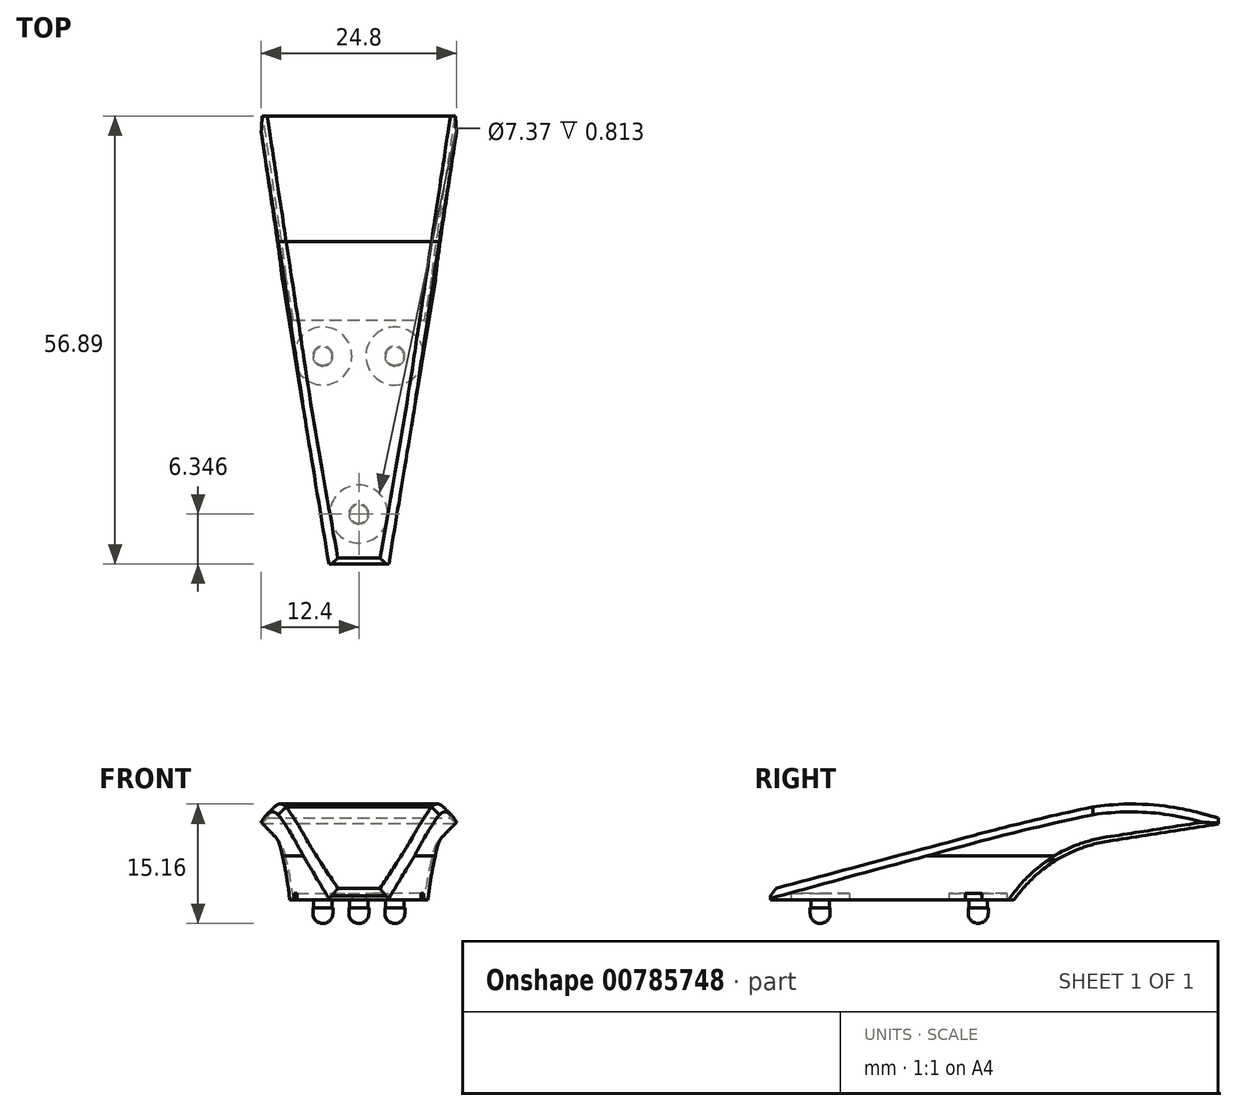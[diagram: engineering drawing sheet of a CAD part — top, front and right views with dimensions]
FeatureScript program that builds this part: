
annotation { "Feature Type Name" : "Feature", "Feature Type Description" : "" }
export const myFeature = defineFeature(function(context is Context, id is Id, definition is map)
    precondition{}
    {
        {
            var Q0;
            Q0=qCreatedBy(makeId("Top.planeOp"),FACE);
            var sketch = newSketch(context, id + "F0", { "sketchPlane" : qUnion([Q0])});
            skPoint(sketch, "E0.middle", {"position": v(0, 0) * mm});
            skLineSegment(sketch, "E1.bottom", {"start": v(3.81, -15.5) * mm, "end": v(-3.8, -15.5) * mm});
            skLineSegment(sketch, "E2", {"start": v(-3.8, -15.5) * mm, "end": v(-8.9, 15.5) * mm});
            skLineSegment(sketch, "E3", {"start": v(3.81, -15.5) * mm, "end": v(8.89, 15.5) * mm});
            skLineSegment(sketch, "E4", {"start": v(-8.9, 15.5) * mm, "end": v(8.89, 15.5) * mm});
            skSolve(sketch);
        }
        {
            var Q0;
            Q0=qCreatedBy(makeId("Front.planeOp"),FACE);
            cPlane(context, id + "F1", {"entities" : qUnion([Q0]), "cplaneType" : CPlaneType.OFFSET, "offset" : 41.4 * mm, "oppositeDirection" : true, "width" : 152.4 * mm, "height" : 152.4 * mm});
        }
        {
            var Q0;
            Q0=qCreatedBy(id+"F1.planeOp",FACE);
            var sketch = newSketch(context, id + "F2", { "sketchPlane" : qUnion([Q0])});
            skLineSegment(sketch, "E5", {"start": v(12.7, 9.65) * mm, "end": v(12.7, 14.22) * mm});
            skLineSegment(sketch, "E6", {"start": v(12.7, 14.22) * mm, "end": v(-12.7, 14.22) * mm});
            skLineSegment(sketch, "E7", {"start": v(-12.7, 14.22) * mm, "end": v(-12.7, 9.65) * mm});
            skLineSegment(sketch, "E8", {"start": v(12.7, 9.65) * mm, "end": v(-12.7, 9.65) * mm});
            skSolve(sketch);
        }
        {
            var Q0;
            Q0 = qSketchRegion(id + "F0", true);
            extrude(context, id + "F3", {"entities" : qUnion([Q0]), "depth" : 5.6 * mm, "offsetDistance" : 25.4 * mm});
        }
        {
            var Q0;
            Q0=makeQuery(id+"F3.opExtrude","CAP_FACE",FACE,{"disambiguationData":[OSD([sQuery(id+"F0.wireOp",EDGE,"E1.bottom"),sQuery(id+"F0.wireOp",EDGE,"E2"),sQuery(id+"F0.wireOp",EDGE,"E3"),sQuery(id+"F0.wireOp",EDGE,"E4")])],"isStart":false});
            var sketch = newSketch(context, id + "F4", { "sketchPlane" : qUnion([Q0])});
            skLineSegment(sketch, "E9", {"start": v(-8.9, 15.5) * mm, "end": v(-3.8, -15.5) * mm});
            skLineSegment(sketch, "E10", {"start": v(-3.8, -15.5) * mm, "end": v(3.81, -15.5) * mm});
            skLineSegment(sketch, "E11", {"start": v(3.81, -15.5) * mm, "end": v(8.89, 15.5) * mm});
            skLineSegment(sketch, "E12", {"start": v(8.89, 15.5) * mm, "end": v(-8.9, 15.5) * mm});
            skSolve(sketch);
        }
        {
            var Q1;
            Q1 = qSketchRegion(id + "F4", true);
            var Q2;
            Q2 = qSketchRegion(id + "F2", true);
            loft(context, id + "F5", {"operationType" : NewBodyOperationType.ADD, "sheetProfilesArray" : [{ "sheetProfileEntities" : qUnion([Q1]) }, { "sheetProfileEntities" : qUnion([Q2]) }]});
        }
        {
            var Q0;
            Q0=makeQuery(id+"F5.opLoft","MID_CAP_EDGE",EDGE,{"disambiguationData":[OSD([sQuery(id+"F2.wireOp",EDGE,"E5"),sQuery(id+"F2.wireOp",EDGE,"E6"),sQuery(id+"F2.wireOp",EDGE,"E7")])],"capPos":1.0});
            chamfer(context, id + "F6", {"entities" : qUnion([Q0]), "chamferType" : ChamferType.OFFSET_ANGLE, "width" : 3.8 * mm, "oppositeDirection" : false, "angle" : 75 * degree, "tangentPropagation" : true});
        }
        {
            var Q0;
            Q0=makeQuery(id+"F5.boolean.opBoolean","MERGE",EDGE,{"derivedFrom":[makeQuery(id+"F3.opExtrude","CAP_EDGE",EDGE,{"disambiguationData":[OSD([sQuery(id+"F0.wireOp",EDGE,"E4")])],"isStart":false}),makeQuery(id+"F5.opLoft","MID_CAP_EDGE",EDGE,{"disambiguationData":[OSD([sQuery(id+"F4.wireOp",EDGE,"E9"),sQuery(id+"F4.wireOp",EDGE,"E11"),sQuery(id+"F4.wireOp",EDGE,"E12")])],"capPos":0.0})]});
            fillet(context, id + "F7", {"entities" : qUnion([Q0]), "radius" : 17.78 * mm, "tangentPropagation" : true, "allowEdgeOverflow" : false});
        }
        {
            var Q0;
            {var subQ0=sQuery(id+"F2.wireOp",EDGE,"E7");var subQ1=sQuery(id+"F2.wireOp",EDGE,"E6");var subQ2=sQuery(id+"F2.wireOp",EDGE,"E5");Q0=makeQuery(id+"F6.opChamfer","BLEND_EDGE",EDGE,{"blendedFrom":[makeQuery(id+"F5.opLoft","MID_CAP_EDGE",EDGE,{"disambiguationData":[OSD([subQ2,subQ1,subQ0])],"capPos":1.0}),makeQuery(id+"F5.opLoft","SWEPT_FACE",FACE,{"disambiguationData":[OSD([subQ2,subQ1,subQ0,sQuery(id+"F4.wireOp",EDGE,"E9"),sQuery(id+"F4.wireOp",EDGE,"E10"),sQuery(id+"F4.wireOp",EDGE,"E11")])]})],"blendedInto":[makeQuery(id+"F5.opLoft","SWEPT_FACE",FACE,{"disambiguationData":[OSD([subQ2,subQ1,subQ0,sQuery(id+"F4.wireOp",EDGE,"E9"),sQuery(id+"F4.wireOp",EDGE,"E10"),sQuery(id+"F4.wireOp",EDGE,"E11")])]})]});}
            fillet(context, id + "F8", {"entities" : qUnion([Q0]), "radius" : 33.02 * mm, "tangentPropagation" : true, "allowEdgeOverflow" : false});
        }
        {
            var Q0;
            Q0=makeQuery(id+"F5.boolean.opBoolean","MERGE",EDGE,{"derivedFrom":[makeQuery(id+"F3.opExtrude","CAP_EDGE",EDGE,{"disambiguationData":[OSD([sQuery(id+"F0.wireOp",EDGE,"E1.bottom")])],"isStart":false}),makeQuery(id+"F5.opLoft","MID_CAP_EDGE",EDGE,{"disambiguationData":[OSD([sQuery(id+"F4.wireOp",EDGE,"E9"),sQuery(id+"F4.wireOp",EDGE,"E10"),sQuery(id+"F4.wireOp",EDGE,"E11")])],"capPos":0.0})]});
            chamfer(context, id + "F9", {"entities" : qUnion([Q0]), "chamferType" : ChamferType.OFFSET_ANGLE, "width" : 4.32 * mm, "oppositeDirection" : false, "angle" : 75 * degree, "tangentPropagation" : true});
        }
        {
            var Q0;
            {var subQ0=sQuery(id+"F4.wireOp",EDGE,"E11");var subQ1=sQuery(id+"F4.wireOp",EDGE,"E10");var subQ2=sQuery(id+"F4.wireOp",EDGE,"E9");Q0=makeQuery(id+"F9.opChamfer","BLEND_EDGE",EDGE,{"blendedFrom":[makeQuery(id+"F5.boolean.opBoolean","MERGE",EDGE,{"derivedFrom":[makeQuery(id+"F3.opExtrude","CAP_EDGE",EDGE,{"disambiguationData":[OSD([sQuery(id+"F0.wireOp",EDGE,"E1.bottom")])],"isStart":false}),makeQuery(id+"F5.opLoft","MID_CAP_EDGE",EDGE,{"disambiguationData":[OSD([subQ2,subQ1,subQ0])],"capPos":0.0})]}),makeQuery(id+"F5.opLoft","SWEPT_FACE",FACE,{"disambiguationData":[OSD([sQuery(id+"F2.wireOp",EDGE,"E5"),sQuery(id+"F2.wireOp",EDGE,"E6"),sQuery(id+"F2.wireOp",EDGE,"E7"),subQ2,subQ1,subQ0])]})],"blendedInto":[makeQuery(id+"F5.opLoft","SWEPT_FACE",FACE,{"disambiguationData":[OSD([sQuery(id+"F2.wireOp",EDGE,"E5"),sQuery(id+"F2.wireOp",EDGE,"E6"),sQuery(id+"F2.wireOp",EDGE,"E7"),subQ2,subQ1,subQ0])]})]});}
            fillet(context, id + "F10", {"entities" : qUnion([Q0]), "radius" : 279.4 * mm, "tangentPropagation" : true, "allowEdgeOverflow" : false});
        }
        {
            var Q0;
            {var subQ0=sQuery(id+"F2.wireOp",EDGE,"E6");var subQ1=sQuery(id+"F2.wireOp",EDGE,"E5");Q0=makeQuery(id+"F6.opChamfer","BLEND_EDGE",EDGE,{"blendedFrom":[makeQuery(id+"F5.opLoft","MID_CAP_EDGE",EDGE,{"disambiguationData":[OSD([subQ1,subQ0,sQuery(id+"F2.wireOp",EDGE,"E7")])],"capPos":1.0}),makeQuery(id+"F5.opLoft","SWEPT_FACE",FACE,{"disambiguationData":[OSD([subQ1,subQ0,sQuery(id+"F2.wireOp",EDGE,"E8"),sQuery(id+"F4.wireOp",EDGE,"E10"),sQuery(id+"F4.wireOp",EDGE,"E11"),sQuery(id+"F4.wireOp",EDGE,"E12")])]})],"blendedInto":[makeQuery(id+"F5.opLoft","SWEPT_FACE",FACE,{"disambiguationData":[OSD([subQ1,subQ0,sQuery(id+"F2.wireOp",EDGE,"E8"),sQuery(id+"F4.wireOp",EDGE,"E10"),sQuery(id+"F4.wireOp",EDGE,"E11"),sQuery(id+"F4.wireOp",EDGE,"E12")])]})]});}
            var Q1;
            {var subQ0=sQuery(id+"F4.wireOp",EDGE,"E11");var subQ1=sQuery(id+"F4.wireOp",EDGE,"E10");var subQ2=sQuery(id+"F2.wireOp",EDGE,"E6");var subQ3=sQuery(id+"F2.wireOp",EDGE,"E5");var subQ4=sQuery(id+"F2.wireOp",EDGE,"E7");Q1=makeQuery(id+"F8.opFillet","BLEND_EDGE",EDGE,{"blendedFrom":[makeQuery(id+"F6.opChamfer","BLEND_EDGE",EDGE,{"blendedFrom":[makeQuery(id+"F5.opLoft","MID_CAP_EDGE",EDGE,{"disambiguationData":[OSD([subQ3,subQ2,subQ4])],"capPos":1.0}),makeQuery(id+"F5.opLoft","SWEPT_FACE",FACE,{"disambiguationData":[OSD([subQ3,subQ2,subQ4,sQuery(id+"F4.wireOp",EDGE,"E9"),subQ1,subQ0])]})],"blendedInto":[makeQuery(id+"F5.opLoft","SWEPT_FACE",FACE,{"disambiguationData":[OSD([subQ3,subQ2,subQ4,sQuery(id+"F4.wireOp",EDGE,"E9"),subQ1,subQ0])]})]}),makeQuery(id+"F5.opLoft","SWEPT_FACE",FACE,{"disambiguationData":[OSD([subQ3,subQ2,sQuery(id+"F2.wireOp",EDGE,"E8"),subQ1,subQ0,sQuery(id+"F4.wireOp",EDGE,"E12")])]})],"blendedInto":[makeQuery(id+"F5.opLoft","SWEPT_FACE",FACE,{"disambiguationData":[OSD([subQ3,subQ2,sQuery(id+"F2.wireOp",EDGE,"E8"),subQ1,subQ0,sQuery(id+"F4.wireOp",EDGE,"E12")])]})]});}
            var Q2;
            {var subQ0=sQuery(id+"F4.wireOp",EDGE,"E10");var subQ1=sQuery(id+"F4.wireOp",EDGE,"E9");var subQ2=sQuery(id+"F2.wireOp",EDGE,"E7");var subQ3=sQuery(id+"F2.wireOp",EDGE,"E6");var subQ4=sQuery(id+"F2.wireOp",EDGE,"E5");Q2=makeQuery(id+"F8.opFillet","BLEND_EDGE",EDGE,{"blendedFrom":[makeQuery(id+"F6.opChamfer","BLEND_EDGE",EDGE,{"blendedFrom":[makeQuery(id+"F5.opLoft","MID_CAP_EDGE",EDGE,{"disambiguationData":[OSD([subQ4,subQ3,subQ2])],"capPos":1.0}),makeQuery(id+"F5.opLoft","SWEPT_FACE",FACE,{"disambiguationData":[OSD([subQ4,subQ3,subQ2,subQ1,subQ0,sQuery(id+"F4.wireOp",EDGE,"E11")])]})],"blendedInto":[makeQuery(id+"F5.opLoft","SWEPT_FACE",FACE,{"disambiguationData":[OSD([subQ4,subQ3,subQ2,subQ1,subQ0,sQuery(id+"F4.wireOp",EDGE,"E11")])]})]}),makeQuery(id+"F5.opLoft","SWEPT_FACE",FACE,{"disambiguationData":[OSD([subQ3,subQ2,sQuery(id+"F2.wireOp",EDGE,"E8"),subQ1,subQ0,sQuery(id+"F4.wireOp",EDGE,"E12")])]})],"blendedInto":[makeQuery(id+"F5.opLoft","SWEPT_FACE",FACE,{"disambiguationData":[OSD([subQ3,subQ2,sQuery(id+"F2.wireOp",EDGE,"E8"),subQ1,subQ0,sQuery(id+"F4.wireOp",EDGE,"E12")])]})]});}
            chamfer(context, id + "F11", {"entities" : qUnion([Q0, Q1, Q2]), "width" : 1.02 * mm, "tangentPropagation" : true});
        }
        {
            var Q0;
            {var subQ0=sQuery(id+"F0.wireOp",EDGE,"E1.bottom");Q0=makeQuery(id+"F9.opChamfer","BLEND_EDGE",EDGE,{"blendedFrom":[makeQuery(id+"F5.boolean.opBoolean","MERGE",EDGE,{"derivedFrom":[makeQuery(id+"F3.opExtrude","CAP_EDGE",EDGE,{"disambiguationData":[OSD([subQ0])],"isStart":false}),makeQuery(id+"F5.opLoft","MID_CAP_EDGE",EDGE,{"disambiguationData":[OSD([sQuery(id+"F4.wireOp",EDGE,"E9"),sQuery(id+"F4.wireOp",EDGE,"E10"),sQuery(id+"F4.wireOp",EDGE,"E11")])],"capPos":0.0})]}),makeQuery(id+"F3.opExtrude","SWEPT_FACE",FACE,{"disambiguationData":[OSD([subQ0])]})],"blendedInto":[makeQuery(id+"F3.opExtrude","SWEPT_FACE",FACE,{"disambiguationData":[OSD([subQ0])]})]});}
            chamfer(context, id + "F12", {"entities" : qUnion([Q0]), "width" : 1.02 * mm, "tangentPropagation" : true});
        }
        {
            var Q0;
            Q0=makeQuery(id+"F7.opFillet","BLEND_EDGE",EDGE,{"blendedFrom":[makeQuery(id+"F5.boolean.opBoolean","MERGE",EDGE,{"derivedFrom":[makeQuery(id+"F3.opExtrude","CAP_EDGE",EDGE,{"disambiguationData":[OSD([sQuery(id+"F0.wireOp",EDGE,"E4")])],"isStart":false}),makeQuery(id+"F5.opLoft","MID_CAP_EDGE",EDGE,{"disambiguationData":[OSD([sQuery(id+"F4.wireOp",EDGE,"E9"),sQuery(id+"F4.wireOp",EDGE,"E11"),sQuery(id+"F4.wireOp",EDGE,"E12")])],"capPos":0.0})]}),makeQuery(id+"F3.opExtrude","SWEPT_FACE",FACE,{"disambiguationData":[OSD([sQuery(id+"F0.wireOp",EDGE,"E2")])]})],"blendedInto":[makeQuery(id+"F3.opExtrude","SWEPT_FACE",FACE,{"disambiguationData":[OSD([sQuery(id+"F0.wireOp",EDGE,"E2")])]})]});
            var Q1;
            Q1=makeQuery(id+"F5.opLoft","SWEPT_EDGE",EDGE,{"disambiguationData":[OSD([sQuery(id+"F2.wireOp",EDGE,"E7"),sQuery(id+"F2.wireOp",EDGE,"E8"),sQuery(id+"F4.wireOp",EDGE,"E9"),sQuery(id+"F4.wireOp",EDGE,"E12")])]});
            var Q2;
            {var subQ0=sQuery(id+"F4.wireOp",EDGE,"E12");var subQ1=sQuery(id+"F4.wireOp",EDGE,"E11");Q2=makeQuery(id+"F7.opFillet","BLEND_EDGE",EDGE,{"blendedFrom":[makeQuery(id+"F5.boolean.opBoolean","MERGE",EDGE,{"derivedFrom":[makeQuery(id+"F3.opExtrude","CAP_EDGE",EDGE,{"disambiguationData":[OSD([sQuery(id+"F0.wireOp",EDGE,"E4")])],"isStart":false}),makeQuery(id+"F5.opLoft","MID_CAP_EDGE",EDGE,{"disambiguationData":[OSD([sQuery(id+"F4.wireOp",EDGE,"E9"),subQ1,subQ0])],"capPos":0.0})]}),makeQuery(id+"F5.opLoft","SWEPT_FACE",FACE,{"disambiguationData":[OSD([sQuery(id+"F2.wireOp",EDGE,"E5"),sQuery(id+"F2.wireOp",EDGE,"E6"),sQuery(id+"F2.wireOp",EDGE,"E8"),sQuery(id+"F4.wireOp",EDGE,"E10"),subQ1,subQ0])]})],"blendedInto":[makeQuery(id+"F5.opLoft","SWEPT_FACE",FACE,{"disambiguationData":[OSD([sQuery(id+"F2.wireOp",EDGE,"E5"),sQuery(id+"F2.wireOp",EDGE,"E6"),sQuery(id+"F2.wireOp",EDGE,"E8"),sQuery(id+"F4.wireOp",EDGE,"E10"),subQ1,subQ0])]})]});}
            var Q3;
            Q3=makeQuery(id+"F7.opFillet","BLEND_EDGE",EDGE,{"blendedFrom":[makeQuery(id+"F5.boolean.opBoolean","MERGE",EDGE,{"derivedFrom":[makeQuery(id+"F3.opExtrude","CAP_EDGE",EDGE,{"disambiguationData":[OSD([sQuery(id+"F0.wireOp",EDGE,"E4")])],"isStart":false}),makeQuery(id+"F5.opLoft","MID_CAP_EDGE",EDGE,{"disambiguationData":[OSD([sQuery(id+"F4.wireOp",EDGE,"E9"),sQuery(id+"F4.wireOp",EDGE,"E11"),sQuery(id+"F4.wireOp",EDGE,"E12")])],"capPos":0.0})]}),makeQuery(id+"F3.opExtrude","SWEPT_FACE",FACE,{"disambiguationData":[OSD([sQuery(id+"F0.wireOp",EDGE,"E3")])]})],"blendedInto":[makeQuery(id+"F3.opExtrude","SWEPT_FACE",FACE,{"disambiguationData":[OSD([sQuery(id+"F0.wireOp",EDGE,"E3")])]})]});
            chamfer(context, id + "F13", {"entities" : qUnion([Q0, Q1, Q2, Q3]), "width" : 0.5 * mm, "tangentPropagation" : true});
        }
        {
            var Q0;
            Q0=makeQuery(id+"F3.opExtrude","CAP_FACE",FACE,{"disambiguationData":[OSD([sQuery(id+"F0.wireOp",EDGE,"E1.bottom"),sQuery(id+"F0.wireOp",EDGE,"E2"),sQuery(id+"F0.wireOp",EDGE,"E3"),sQuery(id+"F0.wireOp",EDGE,"E4")])],"isStart":true});
            var sketch = newSketch(context, id + "F14", { "sketchPlane" : qUnion([Q0])});
            skCircle(sketch, "E13", {"center": v(-4.57, -10.92) * mm, "radius": 3.68 * mm});
            skCircle(sketch, "E14", {"center": v(4.57, -10.92) * mm, "radius": 3.68 * mm});
            skCircle(sketch, "E15", {"center": v(0, 9.14) * mm, "radius": 3.68 * mm});
            skSolve(sketch);
        }
        {
            var Q0;
            Q0=makeQuery(id+"F14.imprint","IMPRINT",FACE,{"disambiguationData":[TD([[makeQuery(id+"F14.imprint","IMPRINT",EDGE,{"derivedFrom":sQuery(id+"F14.wireOp",EDGE,"E15")}),-1.0]])]});
            var sketch = newSketch(context, id + "F15", { "sketchPlane" : qUnion([Q0])});
            skCircle(sketch, "E16", {"center": v(-4.57, -10.92) * mm, "radius": 1.16 * mm});
            skCircle(sketch, "E17", {"center": v(4.57, -10.92) * mm, "radius": 1.16 * mm});
            skCircle(sketch, "E18", {"center": v(0, 9.15) * mm, "radius": 1.16 * mm});
            skSolve(sketch);
        }
        {
            var Q0;
            Q0 = qSketchRegion(id + "F15", true);
            extrude(context, id + "F16", {"entities" : qUnion([Q0]), "operationType" : NewBodyOperationType.ADD, "depth" : 1.02 * mm, "offsetDistance" : 25.4 * mm});
        }
        {
            var Q0;
            Q0=makeQuery(id+"F16.opExtrude","CAP_FACE",FACE,{"disambiguationData":[OSD([sQuery(id+"F15.wireOp",EDGE,"E16")])],"isStart":false});
            var sketch = newSketch(context, id + "F17", { "sketchPlane" : qUnion([Q0])});
            skCircle(sketch, "E19", {"center": v(-4.57, -10.92) * mm, "radius": 1.27 * mm});
            skCircle(sketch, "E20", {"center": v(4.57, -10.92) * mm, "radius": 1.27 * mm});
            skCircle(sketch, "E21", {"center": v(0, 9.15) * mm, "radius": 1.27 * mm});
            skSolve(sketch);
        }
        {
            var Q0;
            Q0 = qSketchRegion(id + "F17", true);
            extrude(context, id + "F18", {"entities" : qUnion([Q0]), "operationType" : NewBodyOperationType.ADD, "depth" : 1.97 * mm, "offsetDistance" : 25.4 * mm});
        }
        {
            var Q0;
            Q0=makeQuery(id+"F18.opExtrude","CAP_EDGE",EDGE,{"disambiguationData":[OSD([sQuery(id+"F17.wireOp",EDGE,"E21")])],"isStart":false});
            var Q1;
            Q1=makeQuery(id+"F18.opExtrude","CAP_EDGE",EDGE,{"disambiguationData":[OSD([sQuery(id+"F17.wireOp",EDGE,"E19")])],"isStart":false});
            var Q2;
            Q2=makeQuery(id+"F18.opExtrude","CAP_EDGE",EDGE,{"disambiguationData":[OSD([sQuery(id+"F17.wireOp",EDGE,"E20")])],"isStart":false});
            fillet(context, id + "F19", {"entities" : qUnion([Q0, Q1, Q2]), "radius" : 1.27 * mm, "tangentPropagation" : true, "allowEdgeOverflow" : false});
        }
        {
            var Q0;
            Q0 = qSketchRegion(id + "F14", true);
            extrude(context, id + "F20", {"entities" : qUnion([Q0]), "operationType" : NewBodyOperationType.REMOVE, "oppositeDirection" : true, "depth" : 0.81 * mm, "offsetDistance" : 25.4 * mm});
        }
    });
